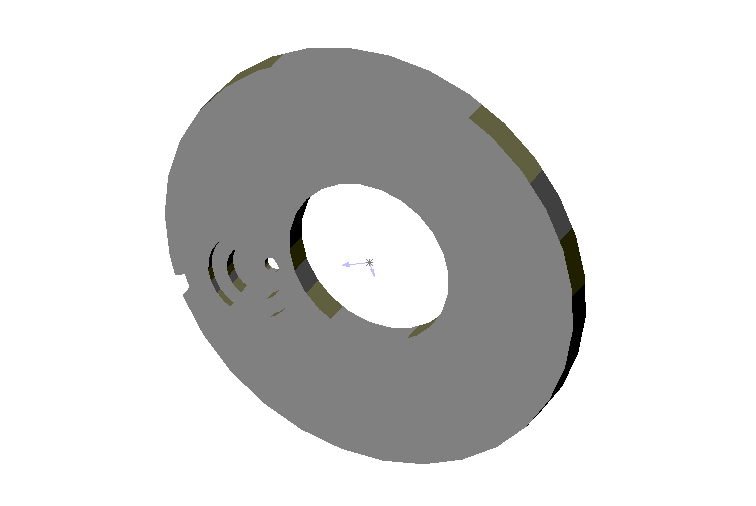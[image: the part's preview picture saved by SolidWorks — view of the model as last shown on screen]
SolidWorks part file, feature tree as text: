
SOLIDWORKS PART (.sldprt)
format: sldprt  version: not decoded by parser v0  size: 127,488 bytes
history: native  units: mm
features: sketch x7, cut_extrude x5, plane x3, extrude x2 + 1 further entry (+6 scaffold rows collapsed)
feature tree (24):
  scaffold x6  (default folders/planes/origin — collapsed)
  "Corps de surface"
  plane  "Plan1"
  plane  "Plan2"
  plane  "Plan3"
  sketch  "Esquisse1"  dims[D1=82.0mm D2=32.0mm]
  extrude  "Base-Extrusion"  Depth=5.3mm
  sketch  "Esquisse2"  dims[D1=77.5mm D2=72.5mm]
  extrude  "Boss.-Extru.1"  Depth=2mm
  sketch  "Esquisse3"  dims[D1=41.0mm]
  cut_extrude  "Enlèv. mat.-Extru.1"  Depth=0.3mm
  sketch  "Esquisse4"  dims[D1=17.0mm D3=32.0mm D2=25.5mm]
  cut_extrude  "Enlèv. mat.-Extru.2"  Depth=1.5mm
  sketch  "Esquisse5"  dims[D1=11.0mm]
  cut_extrude  "Enlèv. mat.-Extru.3"  Depth=2.5mm
  sketch  "Esquisse7"  dims[D1=3.0mm D2=23.0mm]
  cut_extrude  "Enlèv. mat.-Extru.7"  [1 undecoded]
  sketch  "Esquisse8"  dims[D1=37.0mm D2=4.0mm D3=2.0mm]
  cut_extrude  "Enlèv. mat.-Extru.8"  Depth=3mm
decode coverage: 13 of 14 modeling features carry decoded parameters; 1 rows unclassified (native names shown)
note: 1 parameter value undecoded
note: suppression state not decoded; provenance and decode notes live in map.json
